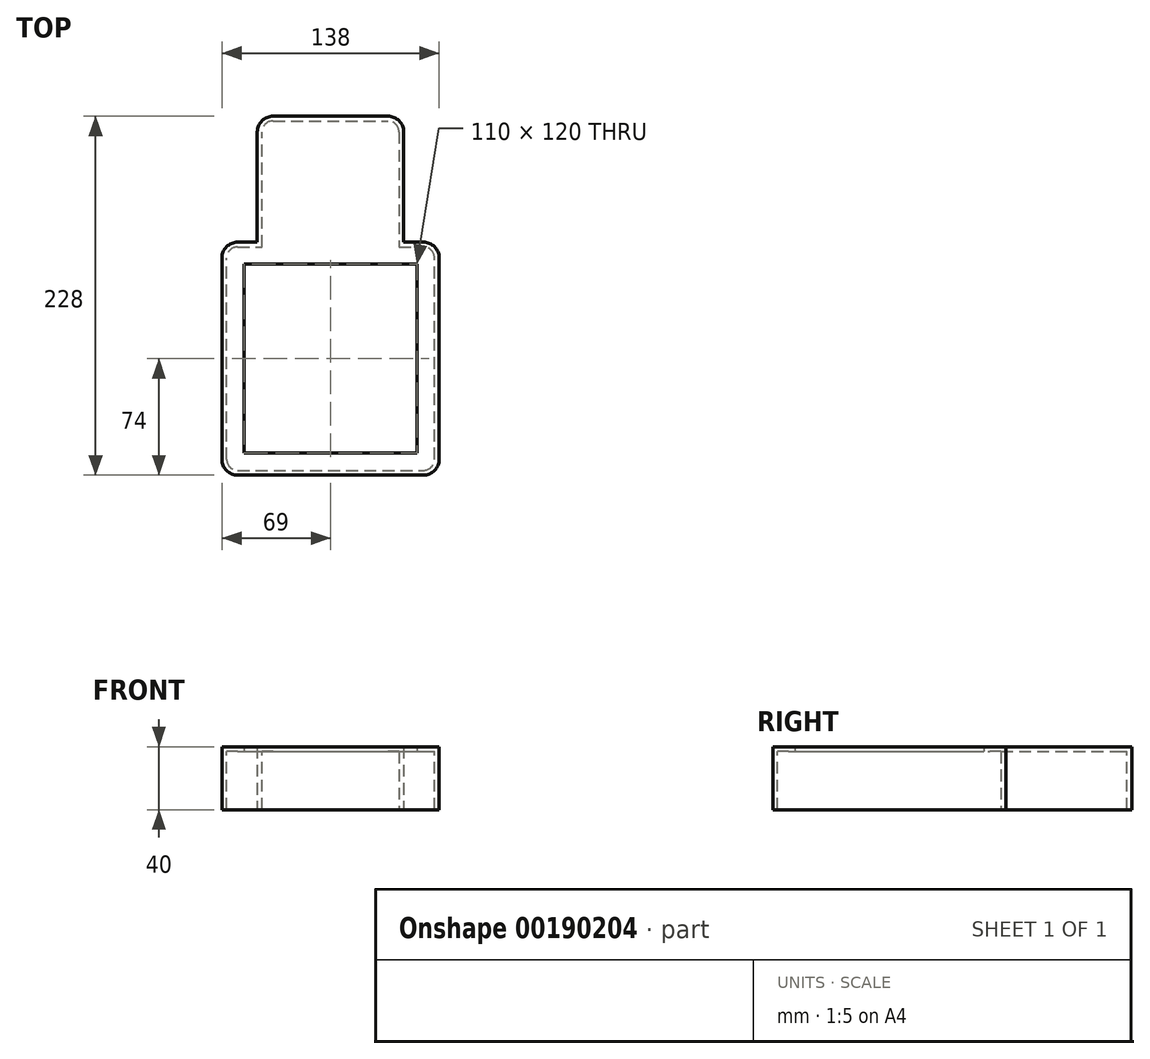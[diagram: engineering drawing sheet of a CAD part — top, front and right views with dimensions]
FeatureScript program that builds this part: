
annotation { "Feature Type Name" : "Feature", "Feature Type Description" : "" }
export const myFeature = defineFeature(function(context is Context, id is Id, definition is map)
    precondition{}
    {
        {
            var Q0;
            Q0=qCreatedBy(makeId("Top.planeOp"),FACE);
            var sketch = newSketch(context, id + "F0", { "sketchPlane" : qUnion([Q0])});
            skLineSegment(sketch, "E0.bottom", {"start": v(-59, -74) * mm, "end": v(59, -74) * mm});
            skLineSegment(sketch, "E0.left", {"start": v(-69, -64) * mm, "end": v(-69, 64) * mm});
            skLineSegment(sketch, "E0.right", {"start": v(69, -64) * mm, "end": v(69, 64) * mm});
            skPoint(sketch, "E0.middle", {"position": v(0, 0) * mm});
            skPoint(sketch, "E1.top.start.orphan", {"position": v(-41.03, -154) * mm});
            skPoint(sketch, "E2.trimOffspring.end.orphan", {"position": v(51.97, -154) * mm});
            skPoint(sketch, "E1.left.start.orphan", {"position": v(-51.97, 154) * mm});
            skPoint(sketch, "E1.right.start.orphan", {"position": v(41.03, 154) * mm});
            skLineSegment(sketch, "E3", {"start": v(-59, 74) * mm, "end": v(-46.5, 74) * mm});
            skLineSegment(sketch, "E4", {"start": v(-46.5, 74) * mm, "end": v(-46.5, 144) * mm});
            skLineSegment(sketch, "E5", {"start": v(-36.5, 154) * mm, "end": v(36.5, 154) * mm});
            skLineSegment(sketch, "E6", {"start": v(46.5, 144) * mm, "end": v(46.5, 74) * mm});
            skLineSegment(sketch, "E7", {"start": v(46.5, 74) * mm, "end": v(59, 74) * mm});
            skPoint(sketch, "E8.visualSharp", {"position": v(-69, 74) * mm});
            skArc(sketch, "E8.filletArc", {"start": v(-59, 74) * mm, "mid": v(-66.07, 71.07) * mm, "end": v(-69, 64) * mm});
            skPoint(sketch, "E9.visualSharp", {"position": v(69, 74) * mm});
            skArc(sketch, "E9.filletArc", {"start": v(69, 64) * mm, "mid": v(66.07, 71.07) * mm, "end": v(59, 74) * mm});
            skPoint(sketch, "E10.visualSharp", {"position": v(46.5, 154) * mm});
            skArc(sketch, "E10.filletArc", {"start": v(46.5, 144) * mm, "mid": v(43.57, 151.07) * mm, "end": v(36.5, 154) * mm});
            skPoint(sketch, "E11.visualSharp", {"position": v(-46.5, 154) * mm});
            skArc(sketch, "E11.filletArc", {"start": v(-36.5, 154) * mm, "mid": v(-43.57, 151.07) * mm, "end": v(-46.5, 144) * mm});
            skPoint(sketch, "E12.visualSharp", {"position": v(-69, -74) * mm});
            skArc(sketch, "E12.filletArc", {"start": v(-69, -64) * mm, "mid": v(-66.07, -71.07) * mm, "end": v(-59, -74) * mm});
            skPoint(sketch, "E13.visualSharp", {"position": v(69, -74) * mm});
            skArc(sketch, "E13.filletArc", {"start": v(59, -74) * mm, "mid": v(66.07, -71.07) * mm, "end": v(69, -64) * mm});
            skSolve(sketch);
        }
        {
            var Q0;
            Q0 = qSketchRegion(id + "F0", true);
            extrude(context, id + "F1", {"entities" : qUnion([Q0]), "depth" : 40 * mm, "offsetDistance" : 25 * mm});
        }
        {
            var Q0;
            Q0=makeQuery(id+"F1.opExtrude","CAP_FACE",FACE,{"disambiguationData":[OSD([sQuery(id+"F0.wireOp",EDGE,"E0.bottom"),sQuery(id+"F0.wireOp",EDGE,"E0.left"),sQuery(id+"F0.wireOp",EDGE,"E0.right"),sQuery(id+"F0.wireOp",EDGE,"E3"),sQuery(id+"F0.wireOp",EDGE,"E4"),sQuery(id+"F0.wireOp",EDGE,"E5"),sQuery(id+"F0.wireOp",EDGE,"E6"),sQuery(id+"F0.wireOp",EDGE,"E7"),sQuery(id+"F0.wireOp",EDGE,"E8.filletArc"),sQuery(id+"F0.wireOp",EDGE,"E9.filletArc"),sQuery(id+"F0.wireOp",EDGE,"E10.filletArc"),sQuery(id+"F0.wireOp",EDGE,"E11.filletArc"),sQuery(id+"F0.wireOp",EDGE,"E12.filletArc"),sQuery(id+"F0.wireOp",EDGE,"E13.filletArc")])],"isStart":true});
            shell(context, id + "F2", {"entities" : qUnion([Q0]), "thickness" : 3 * mm});
        }
        {
            var Q0;
            Q0=makeQuery(id+"F2.opShell","OFFSET_FACE",FACE,{"disambiguationData":[OSD([sQuery(id+"F0.wireOp",EDGE,"E0.bottom"),sQuery(id+"F0.wireOp",EDGE,"E0.left"),sQuery(id+"F0.wireOp",EDGE,"E0.right"),sQuery(id+"F0.wireOp",EDGE,"E3"),sQuery(id+"F0.wireOp",EDGE,"E4"),sQuery(id+"F0.wireOp",EDGE,"E5"),sQuery(id+"F0.wireOp",EDGE,"E6"),sQuery(id+"F0.wireOp",EDGE,"E7"),sQuery(id+"F0.wireOp",EDGE,"E8.filletArc"),sQuery(id+"F0.wireOp",EDGE,"E9.filletArc"),sQuery(id+"F0.wireOp",EDGE,"E10.filletArc"),sQuery(id+"F0.wireOp",EDGE,"E11.filletArc"),sQuery(id+"F0.wireOp",EDGE,"E12.filletArc"),sQuery(id+"F0.wireOp",EDGE,"E13.filletArc")])]});
            var sketch = newSketch(context, id + "F3", { "sketchPlane" : qUnion([Q0])});
            skLineSegment(sketch, "E14.bottom", {"start": v(-55, 60) * mm, "end": v(55, 60) * mm});
            skLineSegment(sketch, "E14.top", {"start": v(-55, -60) * mm, "end": v(55, -60) * mm});
            skLineSegment(sketch, "E14.left", {"start": v(-55, 60) * mm, "end": v(-55, -60) * mm});
            skLineSegment(sketch, "E14.right", {"start": v(55, 60) * mm, "end": v(55, -60) * mm});
            skSolve(sketch);
        }
        {
            var Q0;
            Q0 = qSketchRegion(id + "F3", true);
            extrude(context, id + "F4", {"entities" : qUnion([Q0]), "operationType" : NewBodyOperationType.REMOVE, "oppositeDirection" : true, "depth" : 25 * mm, "offsetDistance" : 25 * mm});
        }
    });
